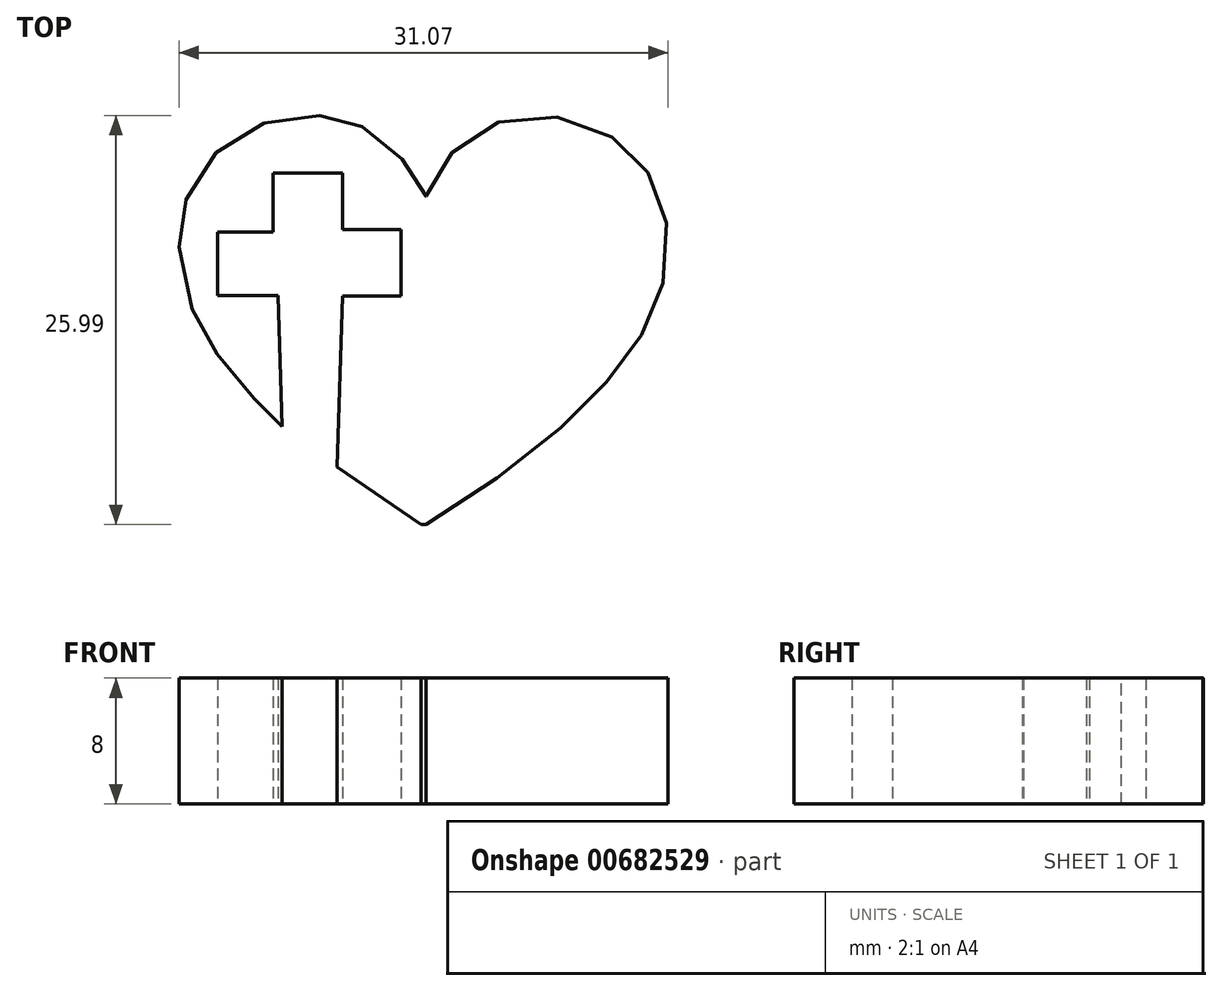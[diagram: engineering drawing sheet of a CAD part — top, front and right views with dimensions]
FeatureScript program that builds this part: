
annotation { "Feature Type Name" : "Feature", "Feature Type Description" : "" }
export const myFeature = defineFeature(function(context is Context, id is Id, definition is map)
    precondition{}
    {
        {
            var Q0;
            Q0=qCreatedBy(makeId("Top.planeOp"),FACE);
            var sketch = newSketch(context, id + "F0", { "sketchPlane" : qUnion([Q0])});
            skLineSegment(sketch, "E0", {"start": v(18.2, 35.8) * mm, "end": v(18.2, 32.2) * mm});
            skLineSegment(sketch, "E1", {"start": v(18.2, 32.2) * mm, "end": v(21.93, 32.2) * mm});
            skLineSegment(sketch, "E2", {"start": v(21.93, 32.2) * mm, "end": v(21.93, 27.96) * mm});
            skLineSegment(sketch, "E3", {"start": v(21.93, 27.96) * mm, "end": v(18.2, 27.96) * mm});
            skLineSegment(sketch, "E4", {"start": v(18.2, 35.8) * mm, "end": v(13.8, 35.8) * mm});
            skLineSegment(sketch, "E5", {"start": v(13.8, 35.8) * mm, "end": v(13.8, 32.04) * mm});
            skLineSegment(sketch, "E6", {"start": v(13.8, 32.04) * mm, "end": v(10.26, 32.04) * mm});
            skLineSegment(sketch, "E7", {"start": v(10.26, 32.04) * mm, "end": v(10.26, 28.02) * mm});
            skLineSegment(sketch, "E8", {"start": v(10.26, 28.02) * mm, "end": v(14.1, 28.02) * mm});
            skLineSegment(sketch, "E9", {"start": v(14.1, 28.02) * mm, "end": v(14.37, 19.7) * mm});
            skLineSegment(sketch, "E10", {"start": v(18.2, 27.96) * mm, "end": v(17.85, 17.13) * mm});
            skFitSpline(sketch, "E11", {"points": [v(14.37, 19.7) * mm, v(13.68, 20.35) * mm, v(12.94, 21.11) * mm, v(11.7, 22.41) * mm, v(10.16, 24.39) * mm, v(9.3, 25.77) * mm, v(8.39, 27.76) * mm, v(7.82, 30.56) * mm, v(7.98, 32.86) * mm, v(8.2, 33.93) * mm, v(9, 35.6) * mm, v(10.52, 37.42) * mm, v(12.45, 38.66) * mm, v(14.37, 39.27) * mm, v(16.63, 39.44) * mm, v(17.67, 39.3) * mm, v(19.1, 38.92) * mm, v(20.95, 37.8) * mm, v(22.04, 36.61) * mm, v(23.33, 34.62) * mm, v(23.44, 34.26) * mm, v(23.75, 34.88) * mm, v(24.75, 36.61) * mm, v(26.53, 38.28) * mm, v(28.34, 39.1) * mm, v(30.69, 39.42) * mm, v(33.18, 39.06) * mm, v(35.27, 38.09) * mm, v(36.2, 37.4) * mm, v(37.72, 35.64) * mm, v(38.48, 34.05) * mm, v(38.88, 31.6) * mm, v(38.62, 29.13) * mm, v(38, 27.14) * mm, v(36.93, 25.05) * mm, v(35.6, 23.27) * mm, v(33.68, 21.12) * mm, v(31.43, 19.07) * mm, v(27.63, 16.15) * mm, v(23.5, 13.46) * mm], "startDerivative": vector(-39.72, 36.66) * mm, "endDerivative": vector(-103.63, -64.62) * mm});
            skLineSegment(sketch, "E12", {"start": v(17.85, 17.13) * mm, "end": v(23.2, 13.46) * mm});
            skLineSegment(sketch, "E13", {"start": v(23.2, 13.46) * mm, "end": v(23.5, 13.46) * mm});
            skLineSegment(sketch, "E14", {"start": v(14.89, 31.16) * mm, "end": v(11.11, 31.16) * mm});
            skLineSegment(sketch, "E15", {"start": v(11.11, 31.16) * mm, "end": v(11.11, 28.75) * mm});
            skLineSegment(sketch, "E16", {"start": v(11.11, 28.75) * mm, "end": v(14.73, 28.75) * mm});
            skLineSegment(sketch, "E17", {"start": v(14.73, 28.75) * mm, "end": v(14.5, 19.4) * mm});
            skLineSegment(sketch, "E18", {"start": v(14.5, 19.4) * mm, "end": v(13.61, 20.14) * mm});
            skLineSegment(sketch, "E19", {"start": v(14.89, 31.16) * mm, "end": v(14.89, 34.78) * mm});
            skLineSegment(sketch, "E20", {"start": v(14.89, 34.78) * mm, "end": v(17.16, 34.78) * mm});
            skLineSegment(sketch, "E21", {"start": v(17.16, 34.78) * mm, "end": v(17.16, 31.16) * mm});
            skLineSegment(sketch, "E22", {"start": v(17.16, 31.16) * mm, "end": v(20.95, 31.16) * mm});
            skLineSegment(sketch, "E23", {"start": v(20.95, 31.16) * mm, "end": v(20.95, 28.88) * mm});
            skLineSegment(sketch, "E24", {"start": v(20.95, 28.88) * mm, "end": v(17.33, 28.88) * mm});
            skLineSegment(sketch, "E25", {"start": v(17.33, 28.88) * mm, "end": v(17.53, 17) * mm});
            skLineSegment(sketch, "E26", {"start": v(17.53, 17) * mm, "end": v(17.53, 16.72) * mm});
            skLineSegment(sketch, "E27", {"start": v(17.53, 16.72) * mm, "end": v(23.2, 13.09) * mm});
            skLineSegment(sketch, "E28", {"start": v(23.2, 13.09) * mm, "end": v(23.5, 12.88) * mm});
            skFitSpline(sketch, "E29", {"points": [v(23.5, 12.88) * mm, v(30.04, 17.38) * mm, v(34.8, 21.36) * mm, v(37.5, 24.5) * mm, v(38.82, 26.78) * mm, v(39.72, 30.03) * mm, v(39.87, 32.03) * mm, v(39.41, 34.52) * mm, v(38.03, 37.04) * mm, v(35.8, 39.1) * mm, v(33.33, 40.23) * mm, v(29.53, 40.56) * mm, v(26.58, 39.7) * mm, v(24.5, 38.09) * mm, v(23.5, 36.76) * mm], "startDerivative": vector(61.17, 40.8) * mm, "endDerivative": vector(-16.95, -26.02) * mm});
            skFitSpline(sketch, "E30", {"points": [v(23.5, 36.76) * mm, v(23.5, 36.61) * mm, v(22.92, 37.4) * mm, v(21.22, 39.1) * mm, v(18.8, 40.24) * mm, v(15.85, 40.55) * mm, v(13.09, 40.07) * mm, v(11.03, 39.1) * mm, v(9, 37.19) * mm, v(7.5, 34.6) * mm, v(7.02, 31.6) * mm, v(7.38, 28.86) * mm, v(8.37, 26.23) * mm, v(9.87, 24) * mm, v(11.7, 21.88) * mm, v(13.61, 20.14) * mm], "startDerivative": vector(1.74, -12.55) * mm, "endDerivative": vector(27.53, -23.7) * mm});
            skSolve(sketch);
        }
        {
            var Q0;
            Q0=makeQuery(id+"F0.imprint","IMPRINT",FACE,{"disambiguationData":[TD([[makeQuery(id+"F0.imprint","IMPRINT",EDGE,{"derivedFrom":sQuery(id+"F0.wireOp",EDGE,"E0")}),1.0]])]});
            extrude(context, id + "F1", {"entities" : qUnion([Q0]), "depth" : 8 * mm, "offsetDistance" : 25 * mm});
        }
    });
